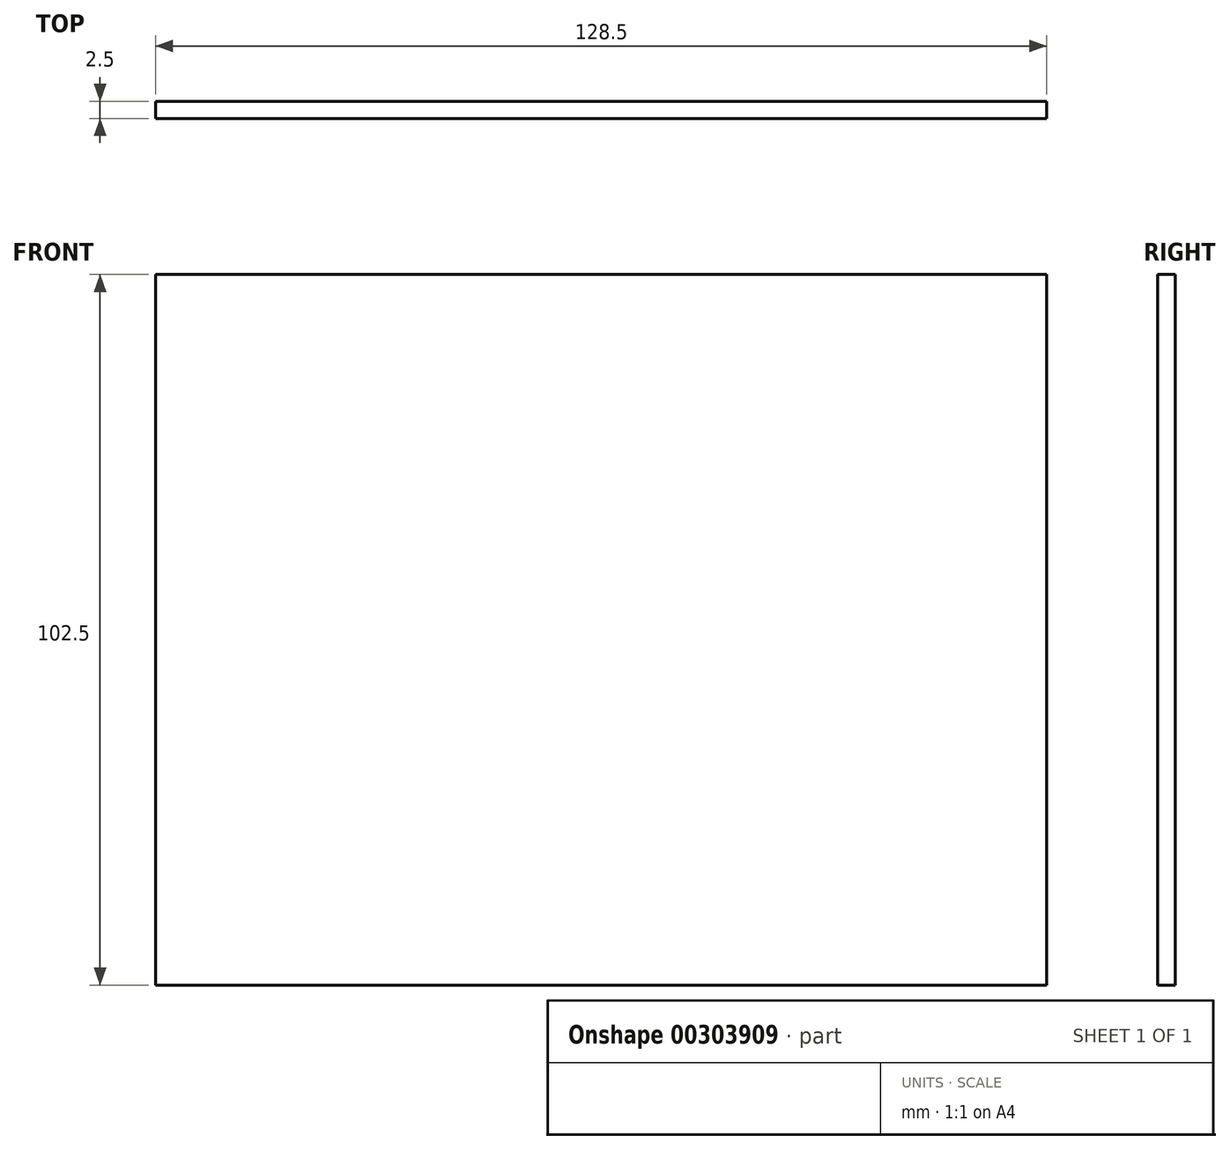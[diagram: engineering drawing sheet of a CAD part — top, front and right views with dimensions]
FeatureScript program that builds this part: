
annotation { "Feature Type Name" : "Feature", "Feature Type Description" : "" }
export const myFeature = defineFeature(function(context is Context, id is Id, definition is map)
    precondition{}
    {
        {
            var Q0;
            Q0=qCreatedBy(makeId("Front.planeOp"),FACE);
            var sketch = newSketch(context, id + "F0", { "sketchPlane" : qUnion([Q0])});
            skLineSegment(sketch, "E0.bottom", {"start": v(64.25, -51.25) * mm, "end": v(-64.25, -51.25) * mm});
            skLineSegment(sketch, "E0.top", {"start": v(64.25, 51.25) * mm, "end": v(-64.25, 51.25) * mm});
            skLineSegment(sketch, "E0.left", {"start": v(64.25, -51.25) * mm, "end": v(64.25, 51.25) * mm});
            skLineSegment(sketch, "E0.right", {"start": v(-64.25, -51.25) * mm, "end": v(-64.25, 51.25) * mm});
            skPoint(sketch, "E0.middle", {"position": v(0, 0) * mm});
            skSolve(sketch);
        }
        {
            var Q0;
            Q0 = qSketchRegion(id + "F0", true);
            extrude(context, id + "F1", {"entities" : qUnion([Q0]), "endBound" : BoundingType.SYMMETRIC, "depth" : 2.5 * mm});
        }
    });
